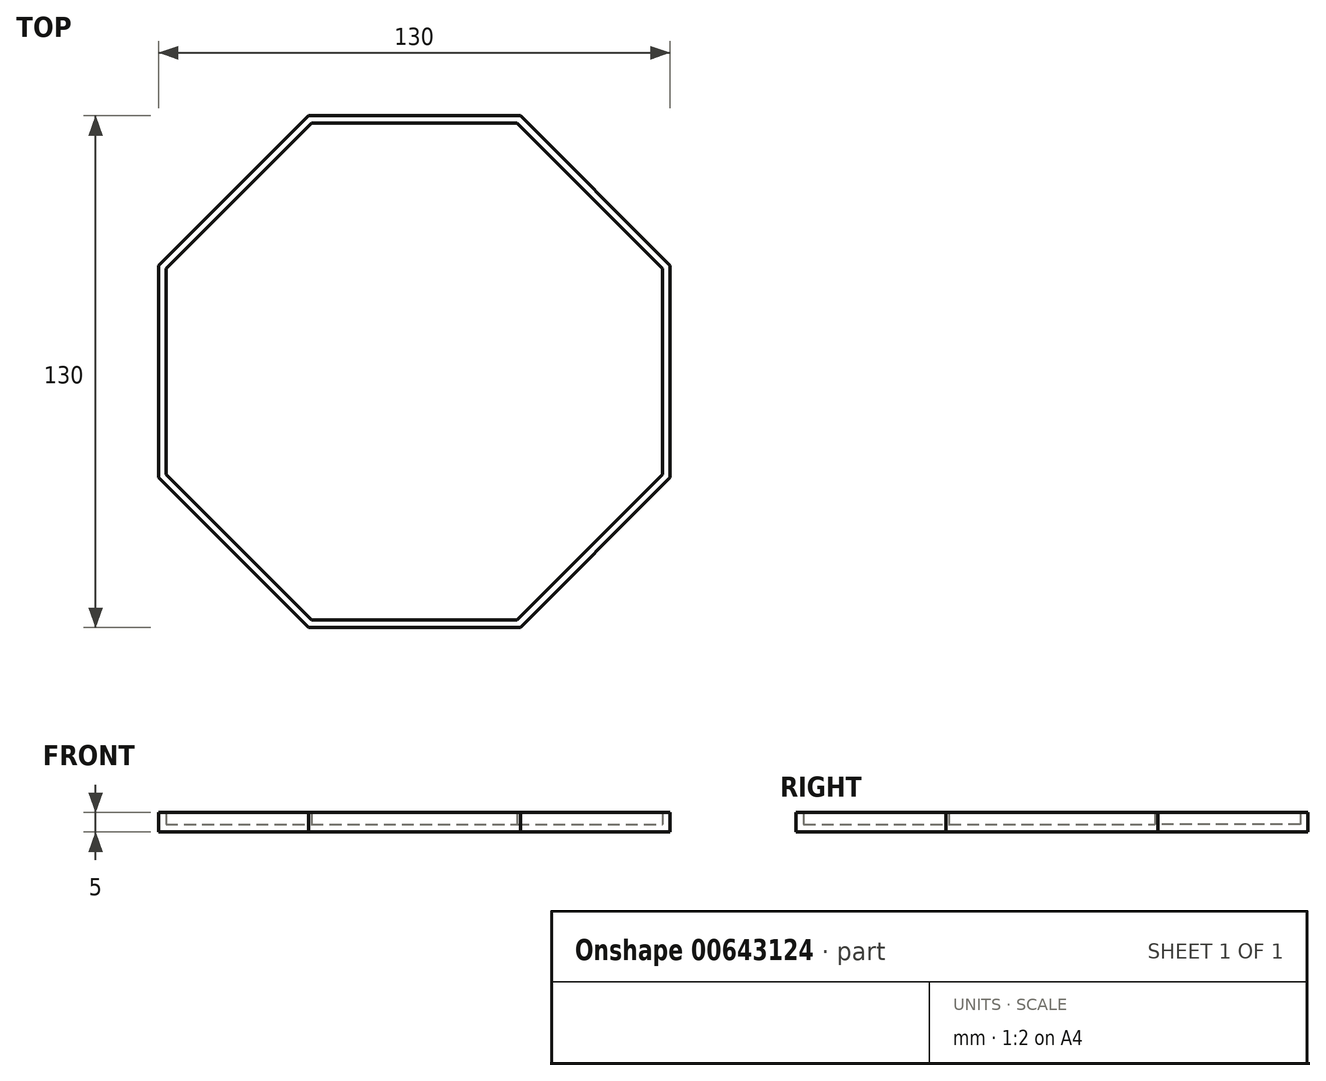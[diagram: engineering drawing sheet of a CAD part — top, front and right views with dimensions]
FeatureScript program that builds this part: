
annotation { "Feature Type Name" : "Feature", "Feature Type Description" : "" }
export const myFeature = defineFeature(function(context is Context, id is Id, definition is map)
    precondition{}
    {
        {
            var Q0;
            Q0=qCreatedBy(makeId("Top.planeOp"),FACE);
            var sketch = newSketch(context, id + "F0", { "sketchPlane" : qUnion([Q0])});
            skLineSegment(sketch, "E0", {"start": v(26.14, 63.1) * mm, "end": v(63.1, 26.14) * mm});
            skLineSegment(sketch, "E1", {"start": v(63.1, 26.14) * mm, "end": v(63.1, -26.14) * mm});
            skLineSegment(sketch, "E2", {"start": v(63.1, -26.14) * mm, "end": v(26.14, -63.1) * mm});
            skLineSegment(sketch, "E3", {"start": v(26.14, -63.1) * mm, "end": v(-26.14, -63.1) * mm});
            skLineSegment(sketch, "E4", {"start": v(-26.14, -63.1) * mm, "end": v(-63.1, -26.14) * mm});
            skLineSegment(sketch, "E5", {"start": v(-63.1, -26.14) * mm, "end": v(-63.1, 26.14) * mm});
            skLineSegment(sketch, "E6", {"start": v(-63.1, 26.14) * mm, "end": v(-26.14, 63.1) * mm});
            skLineSegment(sketch, "E7", {"start": v(-26.14, 63.1) * mm, "end": v(26.14, 63.1) * mm});
            skLineSegment(sketch, "E8", {"start": v(26.92, 65) * mm, "end": v(-26.92, 65) * mm});
            skLineSegment(sketch, "E9", {"start": v(-26.92, 65) * mm, "end": v(-65, 26.92) * mm});
            skLineSegment(sketch, "E10", {"start": v(-65, 26.92) * mm, "end": v(-65, -26.92) * mm});
            skLineSegment(sketch, "E11", {"start": v(-65, -26.92) * mm, "end": v(-26.92, -65) * mm});
            skLineSegment(sketch, "E12", {"start": v(-26.92, -65) * mm, "end": v(26.92, -65) * mm});
            skLineSegment(sketch, "E13", {"start": v(26.92, -65) * mm, "end": v(65, -26.92) * mm});
            skLineSegment(sketch, "E14", {"start": v(65, -26.92) * mm, "end": v(65, 26.92) * mm});
            skLineSegment(sketch, "E15", {"start": v(65, 26.92) * mm, "end": v(26.92, 65) * mm});
            skSolve(sketch);
        }
        {
            var Q0;
            Q0=makeQuery(id+"F0.imprint","IMPRINT",FACE,{"disambiguationData":[TD([[makeQuery(id+"F0.imprint","IMPRINT",EDGE,{"derivedFrom":sQuery(id+"F0.wireOp",EDGE,"E0")}),-1.0]])]});
            extrude(context, id + "F1", {"entities" : qUnion([Q0]), "depth" : 2 * mm, "offsetDistance" : 25 * mm});
        }
        {
            var Q0;
            Q0=makeQuery(id+"F0.imprint","IMPRINT",FACE,{"disambiguationData":[TD([[makeQuery(id+"F0.imprint","IMPRINT",EDGE,{"derivedFrom":sQuery(id+"F0.wireOp",EDGE,"E0")}),1.0]])]});
            extrude(context, id + "F2", {"entities" : qUnion([Q0]), "operationType" : NewBodyOperationType.ADD, "depth" : 5 * mm, "offsetDistance" : 25 * mm});
        }
    });
